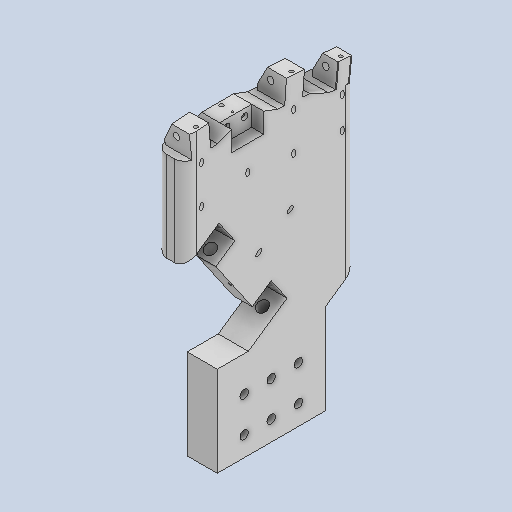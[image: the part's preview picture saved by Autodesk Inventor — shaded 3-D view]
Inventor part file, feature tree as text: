
AUTODESK INVENTOR PART (.ipt)
format: ipt  version: 2024 (Build 280153000, 153)  size: 547,328 bytes
history: native  units: mm
features: sketch x8, extrude x7, other x6, fillet x2, boolean_combine x1
ambient origin geometry x8: Origin, YZ Plane, XZ Plane, XY Plane, X Axis, Y Axis, Z Axis, Center Point
bodies: Solid1 (feature_tree), Solid2 (feature_tree), Solid3 (feature_tree), Solid4 (feature_tree), Solid5 (feature_tree)
feature tree (24):
  other  "handAssembly.iam"
  other  "palm.ipt:1"
  other  "normMale.ipt:2"
  other  "normMale.ipt:4"
  other  "pinkyMale.ipt:1"
  other  "thumbMale.ipt:1"
  boolean_combine  "Combine1"
  extrude  "Extrusion1"  Depth=10.0mm TaperAngle=0.0deg
  sketch  "Sketch2"  dims[d6=15.0mm d7=0.0mm d8=15.0mm d9=0.0mm]
  extrude  "Extrusion2"  Depth=15.0mm TaperAngle=0.0deg
  extrude  "Extrusion3"  TaperAngle=180.0deg  [1 undecoded]
  extrude  "Extrusion4"  Depth=45.0mm
  extrude  "Extrusion5"  Depth=15.0mm TaperAngle=0.0deg
  fillet  "Fillet4"  Radius=5.5mm
  fillet  "Fillet5"  Radius=5.5mm
  extrude  "Extrusion6"  Depth=4.2mm
  extrude  "Extrusion7"  Depth=10.0mm
  sketch  "Sketch1"  dims[d0=10.0mm d1=34.0mm d2=0.0mm]
  sketch  "Sketch3"  dims[d10=15.509mm d11=180.0deg]
  sketch  "Sketch4"  dims[d12=54.0mm d13=45.0mm]
  sketch  "Sketch5"  dims[d14=15.0mm d15=0.0mm d16=15.0mm d17=0.0mm d18=5.5mm d19=5.5mm]
  sketch  "Sketch6"  dims[d24=4.2mm d25=4.2mm]
  sketch  "Sketch7"  dims[d26=4.2mm d27=10.0mm]
  sketch  "Sketch8"  dims[d28=90.0deg d29=4.2mm d30=4.2mm d31=4.2mm d32=15.0mm d33=0.0mm d34=118.0mm d35=0.0mm d4=0.0mm d5=0.0mm]
note: 1 required parameter value undecoded (feature->parameter linkage not recoverable at this tier; creation-order binding heuristic only, values carry confidence <= 0.55)
